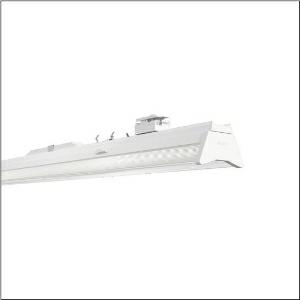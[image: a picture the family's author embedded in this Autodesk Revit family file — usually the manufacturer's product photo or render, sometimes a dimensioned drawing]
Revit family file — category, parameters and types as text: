
# Revit family: licross_r__21_performance_mo_52tm167n485g_c234
name_source: partatom
category: Lighting Fixtures
units: mm (PartAtom-declared; Revit-internal decimal feet)

## family parameters
Cut with Voids When Loaded = No
Host = Face
Light Source = No
Part Type = Normal
Room Calculation Point = No
Round Connector Dimension = Use Diameter
Shared = No

## types (1)
- Licross® 21 Performance MO (1 x LED, 8720 lm, 47.9 W, 4000K)
    Apparent Load = 48 VA
    CIE Flux Codes = 66 88 96 79 100
    Color Rendering = 80
    Color Temperature = 4000K
    Default Elevation = 1800 mm
    Description = Licross® 21 Performance MO, luminaire insert, of sheet steel, galvanised, coil coated, white, length: 1.500mm, width: 120mm, height: 123mm, LED rated luminous flux: 8.720lm, light colour: 840, control gear: ON/OFF, control gear: ECG, with plug, 3-pole, with phase selection, mains connection: 220..240V, AC, 50/60Hz, halogen-free wiring, primary light control with lens, of plastic, primary optical cover: cover, of PMMA, light emission: direct/indirect distribution, primary light characteristic: symmetric, protection rating (complete): IP40, insulation class (complete): insulation class I (protective earthing), certification: CE, ENEC, UKCA, protection symbol: D if used in an environment without relevant dust loads with corresponding accessories, impact resistance: IK06, permissible ambient temperature for indoor applications: -35..+45°C, corresponds to IFS (International Featured Standards) requirements for safety and quality in the food industry, reducing of maximum allowable ambient temperature of 5°C with ceiling mounting, LABS conformity tested according to VDMA 24364:2018-05, packaging unit: 1 piece
    Height = 114 mm
    Lamp = 1 x LED
    Lamp Light Flux = 8720 lm
    Lamp Power = 47.9 W
    Lamp count = 1
    Length = 1500 mm
    Luminous efficacy = 182 lm/W
    Manufacturer = Siteco
    ModVariant = No
    Model = 52TM167N485G
    Mounting Place = Ceiling
    Mounting Type = Pendant
    Number of Poles = 1
    OnlyDefault = Yes
    Power Factor = 1
    Product Name = Licross® 21 Performance MO
    Product group = luminaire insert
    ProductGroupID = 902
    Protection Class = Protection class I
    Protection Degree = IP 40
    RLX_Detail_Level = 1
    RlxData = <blob elided: 30401 chars, md5=1c84faff>
    Socket = socket
    Standby Power = 0 W
    System Light Flux = 8720 lm
    System Power = 48 W
    Type Comments = Product without accessories
    Type Image = l_1256138.jpg
    URL = http://relux.com
    VarID = ---
    Voltage = 0 V
    Weight = 0.00 kg
    Width = 120 mm

## geometry (parser evidence)
native form markers: Blend x4, Sweep x12
no freeform markers — native parametric forms only
